# Revit family: Boiler-Weil_McLain-Simplicity-110MBH_150MBH
name_source: partatom
category: Mechanical Equipment
units: mm (PartAtom-declared; Revit-internal decimal feet)

## family parameters
Cut with Voids When Loaded = No
Host = Face
OmniClass Number = 23.75.10.11.14.14
OmniClass Title = Condensing Boilers
Part Type = Normal
Room Calculation Point = No
Round Connector Dimension = Use Diameter
Shared = No

## types (2) — shared parameters
Boiler In Connection = 0' - 0 3/4"
Boiler In Description = Male NPT
Boiler Out Connection = 0' - 0 3/4"
Boiler Out Description = Male NPT
Condensate Tube Connection = 0' - 0 13/16"
Depth = 1' - 4"
Description = Gas Boiler
Frequency = 60 Hz
Gas Supply Connection Description = Male NPT
Gas Supply Connection Diameter = 1"
Height = 2' - 10"
Hot Water Connection Description = Male NPT
Hot Water Connection Diameter = 1"
Manufacturer = Weil-McLain®
Number of Poles = 1
Phase = 1
Power Factor = 1
Product Name = Simplicity™
URL = https://www.weil-mclain.com
Width = 1' - 8"

## per-type parameters (varying)
| type | Assembly Code | Constraint | Default Elevation | Keynote | Maximum Input Rate | Tank Capacity | Weight |
| 110-C | 23 52 16 | 1 | 0' - 0" | D3010500 | 110000.0 Btu/h | 2.2 gal. | 96 lb. |
| 150-C |  | 2 | 4' - 0" |  | 150000.0 Btu/h | 3.1 gal. | 105 lb. |

note: column(s) folded — value = type name in every type: Model

## geometry (parser evidence)
native form markers: Blend x12, Sweep x2
no freeform markers — native parametric forms only
